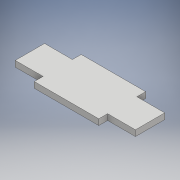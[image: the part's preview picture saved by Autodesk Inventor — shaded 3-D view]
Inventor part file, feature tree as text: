
AUTODESK INVENTOR PART (.ipt)
format: ipt  version: 2018 (Build 220112000, 112)  size: 100,864 bytes
history: native  units: mm
features: extrude x1, sketch x1
ambient origin geometry x8: Origin, YZ Plane, XZ Plane, XY Plane, X Axis, Y Axis, Z Axis, Center Point
bodies: Solid1 (feature_tree)
feature tree (2):
  extrude  "Extrusion1"  Depth=10.0mm
  sketch  "Sketch1"  dims[d0=41.0mm d1=10.0mm d2=22.0mm d3=16.0mm d4=2.0mm d5=0.0mm]
